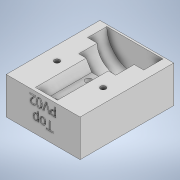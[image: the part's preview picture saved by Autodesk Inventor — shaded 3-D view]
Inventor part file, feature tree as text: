
AUTODESK INVENTOR PART (.ipt)
format: ipt  version: 2022.1 (Build 261234000, 234)  size: 1,006,592 bytes
history: native  units: in
note: dims shown in document units (in); Inventor stores cm internally (conversion verified against a paired STEP export)
features: sketch x6, extrude x5, other x3, boolean_combine x1, hole x1, thicken_offset x1, reference x1
ambient origin geometry x8: Origin, YZ Plane, XZ Plane, XY Plane, X Axis, Y Axis, Z Axis, Center Point
bodies: Solid6 (feature_tree), Solid8 (feature_tree), Solid1 (feature_tree)
feature tree (18):
  boolean_combine  "Combine2"
  extrude  "Extrusion6"  Depth=0.1in TaperAngle=0.0deg
  extrude  "Extrusion7"  Depth=0.1in
  extrude  "Extrusion8"  Depth=0.375in
  extrude  "Extrusion9"  Depth=1.0in
  sketch  "Sketch13"  dims[d47=1.0in d59=0.05in d60=0.0in]
  sketch  "Sketch16"  dims[d61=0.145in d62=0.75in d63=0.3in d64=0.5in d65=0.5635in d66=1.0in d67=0.8108in d70=0.01in d71=0.01in]
  extrude  "Extrusion10"  Depth=0.05in TaperAngle=0.0deg
  hole  "Hole4"  [1 undecoded]
  thicken_offset  "Thicken2"
  sketch  "Sketch9"  dims[d28=0.0in d29=0.0in d30=0.1in d31=0.0in]
  sketch  "Sketch10"  dims[d32=0.0in d33=0.0in d34=0.1in]
  sketch  "Sketch11"  dims[d35=0.0in d36=0.0in d44=0.375in]
  sketch  "Sketch12"  dims[d45=0.375in d46=1.0in]
  reference  "Reference1"
  other  "Solid1:1"
  other  "jigForHexBushing.iam"
  other  "jigForHexBushingForConnectorPieceBottom:1"
note: 1 required parameter value undecoded (feature->parameter linkage not recoverable at this tier; creation-order binding heuristic only, values carry confidence <= 0.55)
